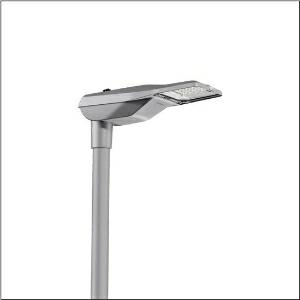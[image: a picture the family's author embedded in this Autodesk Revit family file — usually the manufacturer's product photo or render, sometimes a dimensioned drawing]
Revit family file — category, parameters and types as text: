
# Revit family: streetlight_sl_21_micro___stw1_0a_5xe1e33s08db_cbec
name_source: partatom
category: Lighting Fixtures
units: mm (PartAtom-declared; Revit-internal decimal feet)

## family parameters
Cut with Voids When Loaded = No
Host = Face
Light Source = No
Part Type = Normal
Room Calculation Point = No
Round Connector Dimension = Use Diameter
Shared = No

## types (1)
- --- (1 x LED, 5110 lm, 39.1 W, 3000K)
    Apparent Load = 39 VA
    CIE Flux Codes = 38 75 98 100 100
    Color Rendering = 70
    Color Temperature = 3000K
    Default Elevation = 1800 mm
    Description = Streetlight SL 21 micro, mast luminaire, primary light control with lens, of PMMA, primary optical cover: cover, of toughened safety glass, transparent, light distribution: STW1.0a, light emission: direct distribution, primary light characteristic: asymmetric, installation type: side-entry, post-top, LED, High Power LED, rated luminous flux: 5.110lm, luminous efficacy: 131lm/W, light colour: 730, colour temperature: 3000K, control gear: D4i, control: flexible luminous flux parameterisation, time-dependent luminous flux control, constant luminous flux control, overheat protection, pre-setting: logarithmic dimming characteristic, mains connection: 220..240V, AC, 50/60Hz, start of lifetime: 39W, end of service life: 41W, reduction: 18W, luminaire housing, of diecast aluminium, powder-coated, SITECO metallic grey (DB 702S), corrosivity category C5 high according to DIN EN ISO 12944, please order mast flange separately, inclination adjustable: 0°, 5°, 10°, 15°, sealing non-destructively replaceable, multi-level sealing system, length: 528mm, width: 235mm, height: 110mm, mast flange for spigot size: 42mm (side-entry): 5XC10008XM4, 60/48mm (side-entry/post-top): 5XC10108XM2, 76/60mm (side-entry/post-top): 5XC10108XM1, Smart Interface above, protection rating (complete): IP66, insulation class (complete): insulation class II (safety insulation), certification: CE, ENEC, ENEC+, VDE, impact resistance: IK10, permissible operating ambient temperature for outdoor applications: -40..+50°C, standard-compliant lighting for roads and squares, packaging unit: 1 piece

Light Distribution: STW1.0a
    Height = 110 mm
    Lamp = 1 x LED
    Lamp Light Flux = 5110 lm
    Lamp Power = 39.1 W
    Lamp count = 1
    Length = 528 mm
    Luminous efficacy = 131 lm/W
    Manufacturer = Siteco
    ModVariant = No
    Model = 5XE1E33S08DB
    Number of Poles = 1
    OnlyDefault = Yes
    Power Factor = 1
    Product Name = Streetlight SL 21 micro | STW1.0a
    Product group = mast luminaire | pylon top
    ProductGroupID = 6100
    Protection Class = Protection class II
    Protection Degree = IP 66
    RLX_Detail_Level = 1
    RLX_Emergency_Light_Flux = 0 lm
    RLX_Emergency_Type = 0
    RLX_Emergency_Type_DB = No
    RlxData = <blob elided: 98353 chars, md5=87f7b1a0>
    Socket = socket
    Standby Power = 0 W
    System Light Flux = 5110 lm
    System Power = 39 W
    Type Comments = factory setting: luminous flux: 100 % | dim-lin: 254 | 765 mA
    Type Image = l_1277292.jpg
    URL = http://relux.com
    VarID = @adj_154839
    Voltage = 0 V
    Weight = 0.00 kg
    Width = 235 mm

## geometry (parser evidence)
native form markers: Blend x4, Sweep x9
no freeform markers — native parametric forms only
